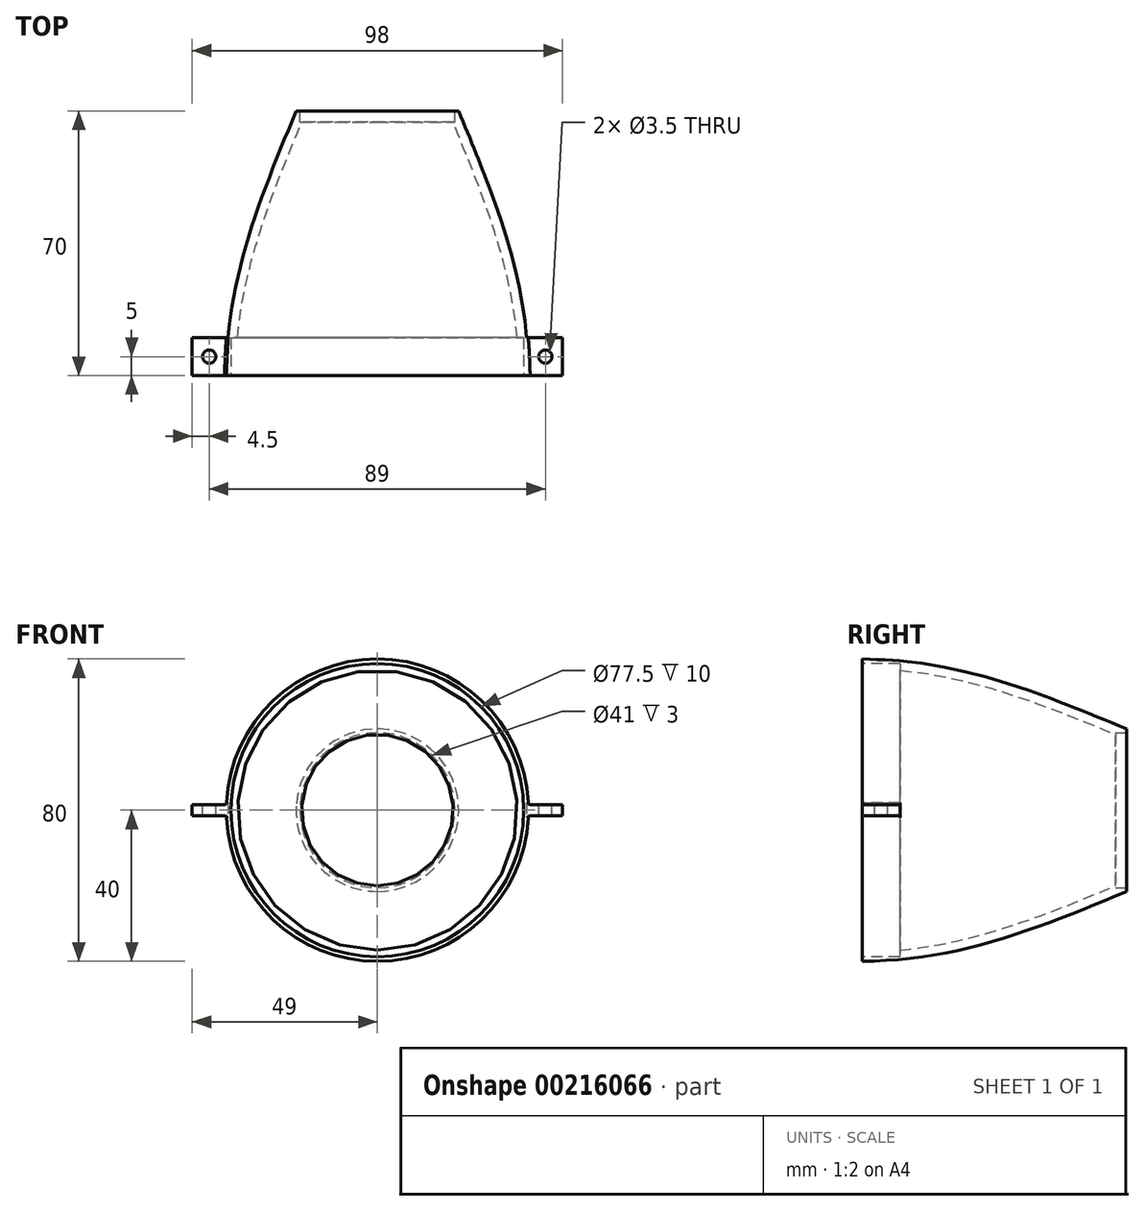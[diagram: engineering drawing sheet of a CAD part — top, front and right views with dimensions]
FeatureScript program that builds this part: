
annotation { "Feature Type Name" : "Feature", "Feature Type Description" : "" }
export const myFeature = defineFeature(function(context is Context, id is Id, definition is map)
    precondition{}
    {
        {
            var Q0;
            Q0=qCreatedBy(makeId("Front.planeOp"),FACE);
            var sketch = newSketch(context, id + "F0", { "sketchPlane" : qUnion([Q0])});
            skCircle(sketch, "E0", {"center": v(0, 0) * mm, "radius": 39.5 * mm});
            skSolve(sketch);
        }
        {
            var Q0;
            Q0=qCreatedBy(makeId("Front.planeOp"),FACE);
            cPlane(context, id + "F1", {"entities" : qUnion([Q0]), "cplaneType" : CPlaneType.OFFSET, "offset" : 60 * mm, "oppositeDirection" : true, "width" : 150 * mm, "height" : 150 * mm});
        }
        {
            var Q0;
            Q0=qCreatedBy(id+"F1.planeOp",FACE);
            var sketch = newSketch(context, id + "F2", { "sketchPlane" : qUnion([Q0])});
            skCircle(sketch, "E1", {"center": v(0, 0) * mm, "radius": 21.5 * mm});
            skSolve(sketch);
        }
        {
            var Q0;
            Q0=qCreatedBy(makeId("Front.planeOp"),FACE);
            cPlane(context, id + "F3", {"entities" : qUnion([Q0]), "cplaneType" : CPlaneType.OFFSET, "offset" : 10 * mm, "width" : 150 * mm, "height" : 150 * mm});
        }
        {
            var Q0;
            Q0=qCreatedBy(id+"F3.planeOp",FACE);
            var sketch = newSketch(context, id + "F4", { "sketchPlane" : qUnion([Q0])});
            skCircle(sketch, "E2", {"center": v(0, 0) * mm, "radius": 40 * mm});
            skSolve(sketch);
        }
        {
            var Q0;
            Q0=makeQuery(id+"F4.imprint","IMPRINT",FACE,{"disambiguationData":[TD([[makeQuery(id+"F4.imprint","IMPRINT",EDGE,{"derivedFrom":sQuery(id+"F4.wireOp",EDGE,"E2")}),1.0]])]});
            var Q1;
            Q1=makeQuery(id+"F0.imprint","IMPRINT",FACE,{"disambiguationData":[TD([[makeQuery(id+"F0.imprint","IMPRINT",EDGE,{"derivedFrom":sQuery(id+"F0.wireOp",EDGE,"E0")}),1.0]])]});
            var Q2;
            Q2=makeQuery(id+"F2.imprint","IMPRINT",FACE,{"disambiguationData":[TD([[makeQuery(id+"F2.imprint","IMPRINT",EDGE,{"derivedFrom":sQuery(id+"F2.wireOp",EDGE,"E1")}),1.0]])]});
            loft(context, id + "F5", {"sheetProfilesArray" : [{ "sheetProfileEntities" : qUnion([Q0]) }, { "sheetProfileEntities" : qUnion([Q1]) }, { "sheetProfileEntities" : qUnion([Q2]) }]});
        }
        {
            var Q0;
            Q0=makeQuery(id+"F5.opLoft","CAP_FACE",FACE,{"disambiguationData":[OSD([makeQuery(id+"F2.imprint","IMPRINT",FACE,{"disambiguationData":[TD([[makeQuery(id+"F2.imprint","IMPRINT",EDGE,{"derivedFrom":sQuery(id+"F2.wireOp",EDGE,"E1")}),1.0]])]})])],"isStart":true});
            var Q1;
            Q1=makeQuery(id+"F5.opLoft","SWEPT_BODY",BODY,{"disambiguationData":[OSD([sQuery(id+"F0.wireOp",EDGE,"E0"),makeQuery(id+"F2.imprint","IMPRINT",FACE,{"disambiguationData":[TD([[makeQuery(id+"F2.imprint","IMPRINT",EDGE,{"derivedFrom":sQuery(id+"F2.wireOp",EDGE,"E1")}),1.0]])]}),makeQuery(id+"F4.imprint","IMPRINT",FACE,{"disambiguationData":[TD([[makeQuery(id+"F4.imprint","IMPRINT",EDGE,{"derivedFrom":sQuery(id+"F4.wireOp",EDGE,"E2")}),1.0]])]})])]});
            shell(context, id + "F6", {"isHollow" : true, "entities" : qUnion([Q0]), "parts" : qUnion([Q1]), "thickness" : 2.5 * mm});
        }
        {
            var Q0;
            Q0=makeQuery(id+"F5.opLoft","CAP_FACE",FACE,{"disambiguationData":[OSD([makeQuery(id+"F4.imprint","IMPRINT",FACE,{"disambiguationData":[TD([[makeQuery(id+"F4.imprint","IMPRINT",EDGE,{"derivedFrom":sQuery(id+"F4.wireOp",EDGE,"E2")}),1.0]])]})])],"isStart":true});
            var sketch = newSketch(context, id + "F7", { "sketchPlane" : qUnion([Q0])});
            skCircle(sketch, "E3", {"center": v(0, 0) * mm, "radius": 38.75 * mm});
            skSolve(sketch);
        }
        {
            var Q0;
            Q0=makeQuery(id+"F7.imprint","IMPRINT",FACE,{"disambiguationData":[TD([[makeQuery(id+"F7.imprint","IMPRINT",EDGE,{"derivedFrom":sQuery(id+"F7.wireOp",EDGE,"E3")}),1.0]])]});
            extrude(context, id + "F8", {"entities" : qUnion([Q0]), "operationType" : NewBodyOperationType.REMOVE, "oppositeDirection" : true, "depth" : 10 * mm});
        }
        {
            var Q0;
            Q0=makeQuery(id+"F5.opLoft","CAP_FACE",FACE,{"disambiguationData":[OSD([makeQuery(id+"F2.imprint","IMPRINT",FACE,{"disambiguationData":[TD([[makeQuery(id+"F2.imprint","IMPRINT",EDGE,{"derivedFrom":sQuery(id+"F2.wireOp",EDGE,"E1")}),1.0]])]})])],"isStart":true});
            var sketch = newSketch(context, id + "F9", { "sketchPlane" : qUnion([Q0])});
            skCircle(sketch, "E4", {"center": v(0, 0) * mm, "radius": 20.5 * mm});
            skSolve(sketch);
        }
        {
            var Q0;
            Q0 = qSketchRegion(id + "F9", true);
            extrude(context, id + "F10", {"entities" : qUnion([Q0]), "operationType" : NewBodyOperationType.REMOVE, "oppositeDirection" : true, "depth" : 3 * mm});
        }
        {
            var Q0;
            Q0=qCreatedBy(makeId("Right.planeOp"),FACE);
            cPlane(context, id + "F11", {"entities" : qUnion([Q0]), "cplaneType" : CPlaneType.OFFSET, "offset" : 49 * mm, "width" : 150 * mm, "height" : 150 * mm});
        }
        {
            var Q0;
            Q0=qCreatedBy(id+"F11.planeOp",FACE);
            var sketch = newSketch(context, id + "F12", { "sketchPlane" : qUnion([Q0])});
            skLineSegment(sketch, "E5.bottom", {"start": v(-10, 1.5) * mm, "end": v(0, 1.5) * mm});
            skLineSegment(sketch, "E5.top", {"start": v(-10, -1.5) * mm, "end": v(0, -1.5) * mm});
            skLineSegment(sketch, "E5.left", {"start": v(-10, 1.5) * mm, "end": v(-10, -1.5) * mm});
            skLineSegment(sketch, "E5.right", {"start": v(0, 1.5) * mm, "end": v(0, -1.5) * mm});
            skSolve(sketch);
        }
        {
            var Q0;
            Q0 = qSketchRegion(id + "F12", true);
            extrude(context, id + "F13", {"entities" : qUnion([Q0]), "operationType" : NewBodyOperationType.ADD, "oppositeDirection" : true, "depth" : 10 * mm});
        }
        {
            var Q0;
            Q0=qCreatedBy(makeId("Right.planeOp"),FACE);
            cPlane(context, id + "F14", {"entities" : qUnion([Q0]), "cplaneType" : CPlaneType.OFFSET, "offset" : 49 * mm, "oppositeDirection" : true, "width" : 150 * mm, "height" : 150 * mm});
        }
        {
            var Q0;
            Q0=qCreatedBy(id+"F14.planeOp",FACE);
            var sketch = newSketch(context, id + "F15", { "sketchPlane" : qUnion([Q0])});
            skLineSegment(sketch, "E6.bottom", {"start": v(0, 1.5) * mm, "end": v(-10, 1.5) * mm});
            skLineSegment(sketch, "E6.top", {"start": v(0, -1.5) * mm, "end": v(-10, -1.5) * mm});
            skLineSegment(sketch, "E6.left", {"start": v(0, 1.5) * mm, "end": v(0, -1.5) * mm});
            skLineSegment(sketch, "E6.right", {"start": v(-10, 1.5) * mm, "end": v(-10, -1.5) * mm});
            skSolve(sketch);
        }
        {
            var Q0;
            Q0 = qSketchRegion(id + "F15", true);
            extrude(context, id + "F16", {"entities" : qUnion([Q0]), "operationType" : NewBodyOperationType.ADD, "depth" : 10 * mm});
        }
        {
            var Q0;
            Q0=makeQuery(id+"F16.boolean.opBoolean","INTERSECT",EDGE,{"derivedFrom":[makeQuery(id+"F5.opLoft","SWEPT_FACE",FACE,{"disambiguationData":[OSD([sQuery(id+"F0.wireOp",EDGE,"E0"),sQuery(id+"F4.wireOp",EDGE,"E2")])]}),makeQuery(id+"F16.opExtrude","SWEPT_FACE",FACE,{"disambiguationData":[OSD([sQuery(id+"F15.wireOp",EDGE,"E6.bottom")])]})]});
            var Q1;
            Q1=makeQuery(id+"F16.boolean.opBoolean","INTERSECT",EDGE,{"derivedFrom":[makeQuery(id+"F5.opLoft","SWEPT_FACE",FACE,{"disambiguationData":[OSD([sQuery(id+"F0.wireOp",EDGE,"E0"),sQuery(id+"F4.wireOp",EDGE,"E2")])]}),makeQuery(id+"F16.opExtrude","SWEPT_FACE",FACE,{"disambiguationData":[OSD([sQuery(id+"F15.wireOp",EDGE,"E6.top")])]})]});
            var Q2;
            Q2=makeQuery(id+"F13.boolean.opBoolean","INTERSECT",EDGE,{"derivedFrom":[makeQuery(id+"F5.opLoft","SWEPT_FACE",FACE,{"disambiguationData":[OSD([sQuery(id+"F0.wireOp",EDGE,"E0"),sQuery(id+"F4.wireOp",EDGE,"E2")])]}),makeQuery(id+"F13.opExtrude","SWEPT_FACE",FACE,{"disambiguationData":[OSD([sQuery(id+"F12.wireOp",EDGE,"E5.top")])]})]});
            var Q3;
            Q3=makeQuery(id+"F13.boolean.opBoolean","INTERSECT",EDGE,{"derivedFrom":[makeQuery(id+"F5.opLoft","SWEPT_FACE",FACE,{"disambiguationData":[OSD([sQuery(id+"F0.wireOp",EDGE,"E0"),sQuery(id+"F4.wireOp",EDGE,"E2")])]}),makeQuery(id+"F13.opExtrude","SWEPT_FACE",FACE,{"disambiguationData":[OSD([sQuery(id+"F12.wireOp",EDGE,"E5.bottom")])]})]});
            fillet(context, id + "F17", {"entities" : qUnion([Q0, Q1, Q2, Q3]), "radius" : .5 * mm, "tangentPropagation" : true, "allowEdgeOverflow" : false});
        }
        {
            var Q0;
            Q0=makeQuery(id+"F16.opExtrude","SWEPT_FACE",FACE,{"disambiguationData":[OSD([sQuery(id+"F15.wireOp",EDGE,"E6.bottom")])]});
            var sketch = newSketch(context, id + "F18", { "sketchPlane" : qUnion([Q0])});
            skCircle(sketch, "E7", {"center": v(-44.5, -5) * mm, "radius": 1.75 * mm});
            skPoint(sketch, "E7.centerSnap0", {"position": v(-44.5, 0) * mm});
            skCircle(sketch, "E8.MirrorC", {"center": v(44.5, -5) * mm, "radius": 1.75 * mm});
            skSolve(sketch);
        }
        {
            var Q0;
            Q0 = qSketchRegion(id + "F18", true);
            extrude(context, id + "F19", {"entities" : qUnion([Q0]), "operationType" : NewBodyOperationType.REMOVE, "endBound" : BoundingType.THROUGH_ALL, "oppositeDirection" : true, "depth" : 25 * mm});
        }
    });
